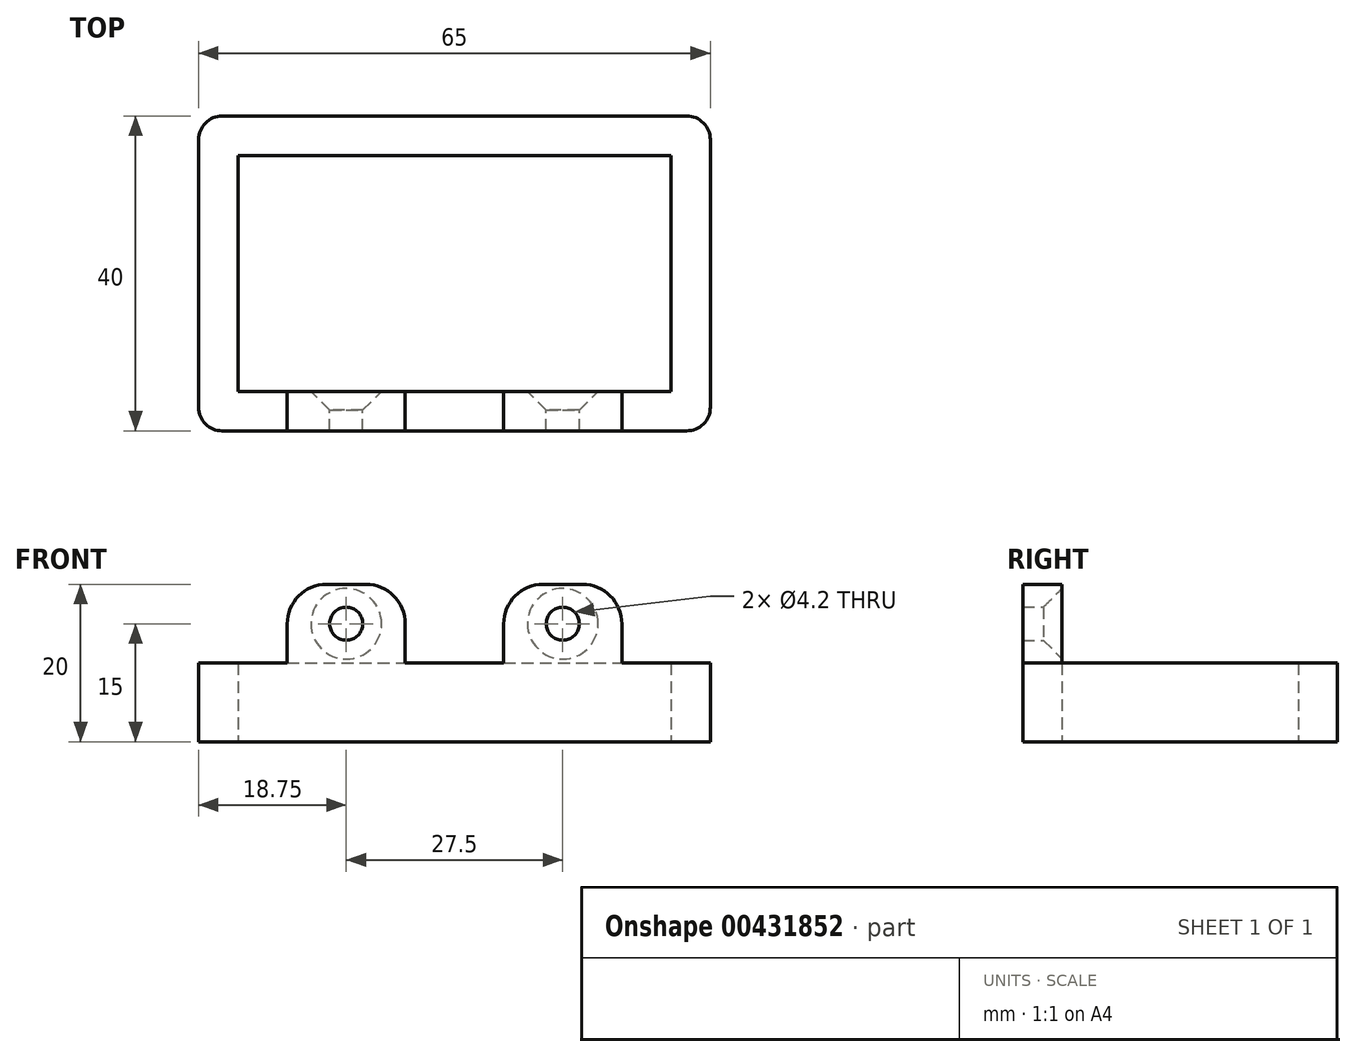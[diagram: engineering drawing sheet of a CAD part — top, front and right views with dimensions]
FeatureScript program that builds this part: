
annotation { "Feature Type Name" : "Feature", "Feature Type Description" : "" }
export const myFeature = defineFeature(function(context is Context, id is Id, definition is map)
    precondition{}
    {
        {
            var Q0;
            Q0=qCreatedBy(makeId("Top.planeOp"),FACE);
            var sketch = newSketch(context, id + "F0", { "sketchPlane" : qUnion([Q0])});
            skLineSegment(sketch, "E0.bottom", {"start": v(-29.5, 20) * mm, "end": v(29.5, 20) * mm});
            skLineSegment(sketch, "E0.top", {"start": v(-29.5, -20) * mm, "end": v(29.5, -20) * mm});
            skLineSegment(sketch, "E0.left", {"start": v(-32.5, 17) * mm, "end": v(-32.5, -17) * mm});
            skLineSegment(sketch, "E0.right", {"start": v(32.5, 17) * mm, "end": v(32.5, -17) * mm});
            skPoint(sketch, "E1.visualSharp", {"position": v(-32.5, 20) * mm});
            skArc(sketch, "E1.filletArc", {"start": v(-29.5, 20) * mm, "mid": v(-31.62, 19.12) * mm, "end": v(-32.5, 17) * mm});
            skPoint(sketch, "E2.visualSharp", {"position": v(-32.5, -20) * mm});
            skArc(sketch, "E2.filletArc", {"start": v(-32.5, -17) * mm, "mid": v(-31.62, -19.12) * mm, "end": v(-29.5, -20) * mm});
            skPoint(sketch, "E3.visualSharp", {"position": v(32.5, -20) * mm});
            skArc(sketch, "E3.filletArc", {"start": v(29.5, -20) * mm, "mid": v(31.62, -19.12) * mm, "end": v(32.5, -17) * mm});
            skPoint(sketch, "E4.visualSharp", {"position": v(32.5, 20) * mm});
            skArc(sketch, "E4.filletArc", {"start": v(32.5, 17) * mm, "mid": v(31.62, 19.12) * mm, "end": v(29.5, 20) * mm});
            skLineSegment(sketch, "E5.0", {"start": v(-27.5, 15) * mm, "end": v(27.5, 15) * mm});
            skLineSegment(sketch, "E5.1", {"start": v(-27.5, 15) * mm, "end": v(-27.5, -15) * mm});
            skLineSegment(sketch, "E5.2", {"start": v(-27.5, -15) * mm, "end": v(27.5, -15) * mm});
            skLineSegment(sketch, "E5.3", {"start": v(27.5, 15) * mm, "end": v(27.5, -15) * mm});
            skSolve(sketch);
        }
        {
            var Q0;
            Q0=makeQuery(id+"F0.imprint","IMPRINT",FACE,{"disambiguationData":[TD([[makeQuery(id+"F0.imprint","IMPRINT",EDGE,{"derivedFrom":sQuery(id+"F0.wireOp",EDGE,"E0.bottom")}),-1.0]])]});
            extrude(context, id + "F1", {"entities" : qUnion([Q0]), "depth" : 10 * mm});
        }
        {
            var Q0;
            Q0=makeQuery(id+"F1.opExtrude","CAP_FACE",FACE,{"disambiguationData":[OSD([sQuery(id+"F0.wireOp",EDGE,"E0.bottom"),sQuery(id+"F0.wireOp",EDGE,"E0.top"),sQuery(id+"F0.wireOp",EDGE,"E0.left"),sQuery(id+"F0.wireOp",EDGE,"E0.right"),sQuery(id+"F0.wireOp",EDGE,"E1.filletArc"),sQuery(id+"F0.wireOp",EDGE,"E2.filletArc"),sQuery(id+"F0.wireOp",EDGE,"E3.filletArc"),sQuery(id+"F0.wireOp",EDGE,"E4.filletArc"),sQuery(id+"F0.wireOp",EDGE,"E5.0"),sQuery(id+"F0.wireOp",EDGE,"E5.1"),sQuery(id+"F0.wireOp",EDGE,"E5.2"),sQuery(id+"F0.wireOp",EDGE,"E5.3")])],"isStart":false});
            var sketch = newSketch(context, id + "F2", { "sketchPlane" : qUnion([Q0])});
            skLineSegment(sketch, "E6", {"start": v(27.5, -15) * mm, "end": v(0, -15) * mm, "construction": true});
            skLineSegment(sketch, "E7", {"start": v(0, -15) * mm, "end": v(-27.5, -15) * mm, "construction": true});
            skLineSegment(sketch, "E8", {"start": v(-13.75, -15) * mm, "end": v(-13.75, -20) * mm, "construction": true});
            skLineSegment(sketch, "E9", {"start": v(13.75, -15) * mm, "end": v(13.75, -20) * mm, "construction": true});
            skLineSegment(sketch, "E10.bottom", {"start": v(-21.25, -15) * mm, "end": v(-6.25, -15) * mm});
            skLineSegment(sketch, "E10.top", {"start": v(-21.25, -20) * mm, "end": v(-6.25, -20) * mm});
            skLineSegment(sketch, "E10.left", {"start": v(-21.25, -15) * mm, "end": v(-21.25, -20) * mm});
            skLineSegment(sketch, "E10.right", {"start": v(-6.25, -15) * mm, "end": v(-6.25, -20) * mm});
            skLineSegment(sketch, "E11.bottom", {"start": v(6.25, -15) * mm, "end": v(21.25, -15) * mm});
            skLineSegment(sketch, "E11.top", {"start": v(6.25, -20) * mm, "end": v(21.25, -20) * mm});
            skLineSegment(sketch, "E11.left", {"start": v(6.25, -15) * mm, "end": v(6.25, -20) * mm});
            skLineSegment(sketch, "E11.right", {"start": v(21.25, -15) * mm, "end": v(21.25, -20) * mm});
            skSolve(sketch);
        }
        {
            var Q0;
            Q0=makeQuery(id+"F2.imprint","IMPRINT",FACE,{"disambiguationData":[TD([[makeQuery(id+"F2.imprint","IMPRINT",EDGE,{"derivedFrom":sQuery(id+"F2.wireOp",EDGE,"E10.bottom")}),-1.0]])]});
            var Q1;
            Q1=makeQuery(id+"F2.imprint","IMPRINT",FACE,{"disambiguationData":[TD([[makeQuery(id+"F2.imprint","IMPRINT",EDGE,{"derivedFrom":sQuery(id+"F2.wireOp",EDGE,"E11.bottom")}),-1.0]])]});
            extrude(context, id + "F3", {"entities" : qUnion([Q0, Q1]), "operationType" : NewBodyOperationType.ADD, "depth" : 10 * mm});
        }
        {
            var Q0;
            Q0=makeQuery(id+"F3.opExtrude","CAP_EDGE",EDGE,{"disambiguationData":[OSD([sQuery(id+"F2.wireOp",EDGE,"E10.left")])],"isStart":false});
            var Q1;
            Q1=makeQuery(id+"F3.opExtrude","CAP_EDGE",EDGE,{"disambiguationData":[OSD([sQuery(id+"F2.wireOp",EDGE,"E10.right")])],"isStart":false});
            var Q2;
            Q2=makeQuery(id+"F3.opExtrude","CAP_EDGE",EDGE,{"disambiguationData":[OSD([sQuery(id+"F2.wireOp",EDGE,"E11.left")])],"isStart":false});
            var Q3;
            Q3=makeQuery(id+"F3.opExtrude","CAP_EDGE",EDGE,{"disambiguationData":[OSD([sQuery(id+"F2.wireOp",EDGE,"E11.right")])],"isStart":false});
            fillet(context, id + "F4", {"entities" : qUnion([Q0, Q1, Q2, Q3]), "radius" : 5 * mm, "tangentPropagation" : true, "allowEdgeOverflow" : false});
        }
        {
            var Q0;
            Q0=makeQuery(id+"F3.boolean.opBoolean","MERGE",FACE,{"derivedFrom":[makeQuery(id+"F1.opExtrude","SWEPT_FACE",FACE,{"disambiguationData":[OSD([sQuery(id+"F0.wireOp",EDGE,"E5.2")])]}),makeQuery(id+"F3.opExtrude","SWEPT_FACE",FACE,{"disambiguationData":[OSD([sQuery(id+"F2.wireOp",EDGE,"E10.bottom")])]}),makeQuery(id+"F3.opExtrude","SWEPT_FACE",FACE,{"disambiguationData":[OSD([sQuery(id+"F2.wireOp",EDGE,"E11.bottom")])]})]});
            var sketch = newSketch(context, id + "F5", { "sketchPlane" : qUnion([Q0])});
            skLineSegment(sketch, "E12", {"start": v(21.25, 10) * mm, "end": v(6.25, 10) * mm, "construction": true});
            skLineSegment(sketch, "E13", {"start": v(13.75, 10) * mm, "end": v(13.75, 20) * mm, "construction": true});
            skPoint(sketch, "E14", {"position": v(13.75, 15) * mm});
            skPoint(sketch, "E15.MirrorP", {"position": v(-13.75, 15) * mm});
            skSolve(sketch);
        }
        {
            var Q0;
            Q0=sQuery(id+"F5.wireOp",VERTEX,"E14");
            var Q1;
            Q1=sQuery(id+"F5.wireOp",VERTEX,"E15.MirrorP");
            var Q2;
            Q2=makeQuery(id+"F1.opExtrude","SWEPT_BODY",BODY,{"disambiguationData":[OSD([sQuery(id+"F0.wireOp",EDGE,"E0.bottom"),sQuery(id+"F0.wireOp",EDGE,"E0.top"),sQuery(id+"F0.wireOp",EDGE,"E0.left"),sQuery(id+"F0.wireOp",EDGE,"E0.right"),sQuery(id+"F0.wireOp",EDGE,"E1.filletArc"),sQuery(id+"F0.wireOp",EDGE,"E2.filletArc"),sQuery(id+"F0.wireOp",EDGE,"E3.filletArc"),sQuery(id+"F0.wireOp",EDGE,"E4.filletArc"),sQuery(id+"F0.wireOp",EDGE,"E5.0"),sQuery(id+"F0.wireOp",EDGE,"E5.1"),sQuery(id+"F0.wireOp",EDGE,"E5.2"),sQuery(id+"F0.wireOp",EDGE,"E5.3")])]});
            hole(context, id + "F6", {"style" : HoleStyle.C_SINK, "endStyle" : HoleEndStyle.THROUGH, "holeDiameter" : 4.2 * mm, "cSinkDiameter" : 8.96 * mm, "cSinkAngle" : 90 * degree, "isTappedThrough" : true, "tappedDepth" : 12 * mm, "tapClearance" : 3, "locations" : qUnion([Q0, Q1]), "scope" : qUnion([Q2])});
        }
    });
